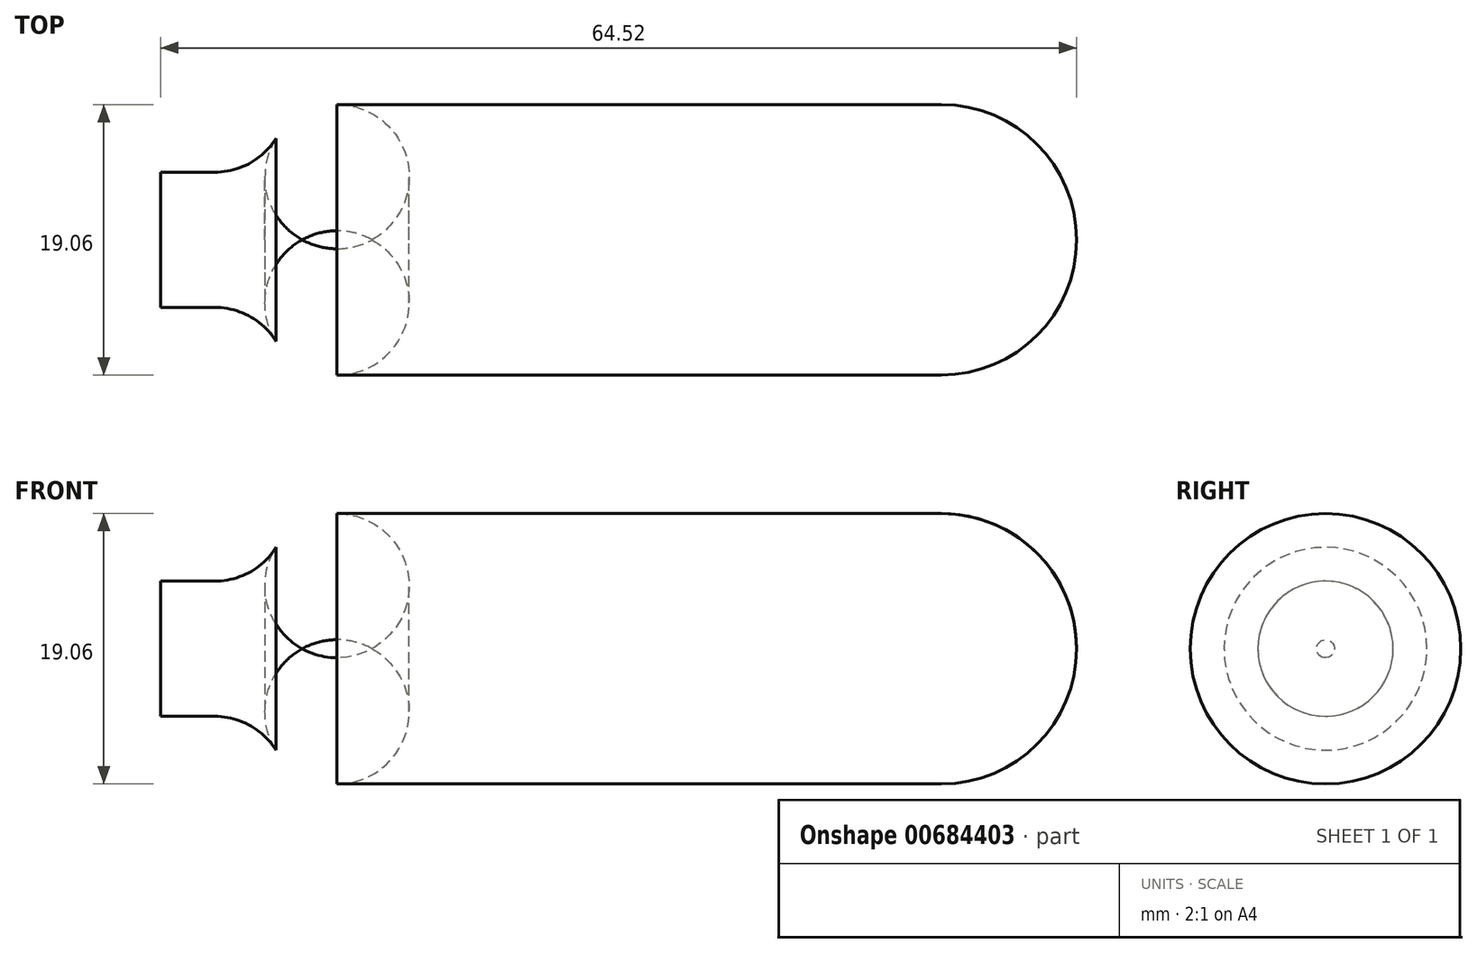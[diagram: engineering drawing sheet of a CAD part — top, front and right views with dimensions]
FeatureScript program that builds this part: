
annotation { "Feature Type Name" : "Feature", "Feature Type Description" : "" }
export const myFeature = defineFeature(function(context is Context, id is Id, definition is map)
    precondition{}
    {
        {
            var Q0;
            Q0=qCreatedBy(makeId("Front.planeOp"),FACE);
            var sketch = newSketch(context, id + "F0", { "sketchPlane" : qUnion([Q0])});
            skLineSegment(sketch, "E0", {"start": v(0, 0) * mm, "end": v(64.52, 0) * mm});
            skLineSegment(sketch, "E1", {"start": v(0, 0) * mm, "end": v(0, 4.76) * mm});
            skLineSegment(sketch, "E2", {"start": v(64.52, 0) * mm, "end": v(64.52, 9.53) * mm});
            skLineSegment(sketch, "E3", {"start": v(8.9, 9.52) * mm, "end": v(64.52, 9.52) * mm});
            skLineSegment(sketch, "E4", {"start": v(0, 4.76) * mm, "end": v(8.9, 4.76) * mm});
            skLineSegment(sketch, "E5", {"start": v(8.9, 4.76) * mm, "end": v(8.9, 9.52) * mm});
            skPoint(sketch, "E6.orphan", {"position": v(0, 9.52) * mm});
            skSolve(sketch);
        }
        {
            var Q0;
            Q0=makeQuery(id+"F0.imprint","IMPRINT",FACE,{"disambiguationData":[TD([[makeQuery(id+"F0.imprint","IMPRINT",EDGE,{"derivedFrom":sQuery(id+"F0.wireOp",EDGE,"E0")}),1.0]])]});
            var Q1;
            Q1=sQuery(id+"F0.wireOp",EDGE,"E0");
            revolve(context, id + "F1", {"entities" : qUnion([Q0]), "axis" : qUnion([Q1]), "revolveType" : RevolveType.FULL});
        }
        {
            var Q0;
            Q0=makeQuery(id+"F1.opRevolve","SWEPT_EDGE",EDGE,{"disambiguationData":[OSD([sQuery(id+"F0.wireOp",EDGE,"E2"),sQuery(id+"F0.wireOp",EDGE,"E3")])]});
            fillet(context, id + "F2", {"entities" : qUnion([Q0]), "radius" : 9.52 * mm, "tangentPropagation" : true, "allowEdgeOverflow" : false});
        }
        {
            var Q0;
            Q0=makeQuery(id+"F1.opRevolve","SWEPT_EDGE",EDGE,{"disambiguationData":[OSD([sQuery(id+"F0.wireOp",EDGE,"E4"),sQuery(id+"F0.wireOp",EDGE,"E5")])]});
            fillet(context, id + "F3", {"entities" : qUnion([Q0]), "radius" : 5.08 * mm, "tangentPropagation" : true, "allowEdgeOverflow" : false});
        }
        {
            var Q0;
            Q0=makeQuery(id+"F3.opFillet","BLEND_EDGE",EDGE,{"blendedFrom":[makeQuery(id+"F1.opRevolve","SWEPT_EDGE",EDGE,{"disambiguationData":[OSD([sQuery(id+"F0.wireOp",EDGE,"E4"),sQuery(id+"F0.wireOp",EDGE,"E5")])]}),makeQuery(id+"F1.opRevolve","SWEPT_FACE",FACE,{"disambiguationData":[OSD([sQuery(id+"F0.wireOp",EDGE,"E3")])]})],"blendedInto":[makeQuery(id+"F1.opRevolve","SWEPT_FACE",FACE,{"disambiguationData":[OSD([sQuery(id+"F0.wireOp",EDGE,"E3")])]})]});
            fillet(context, id + "F4", {"entities" : qUnion([Q0]), "radius" : 5.08 * mm, "tangentPropagation" : true, "allowEdgeOverflow" : false});
        }
    });
